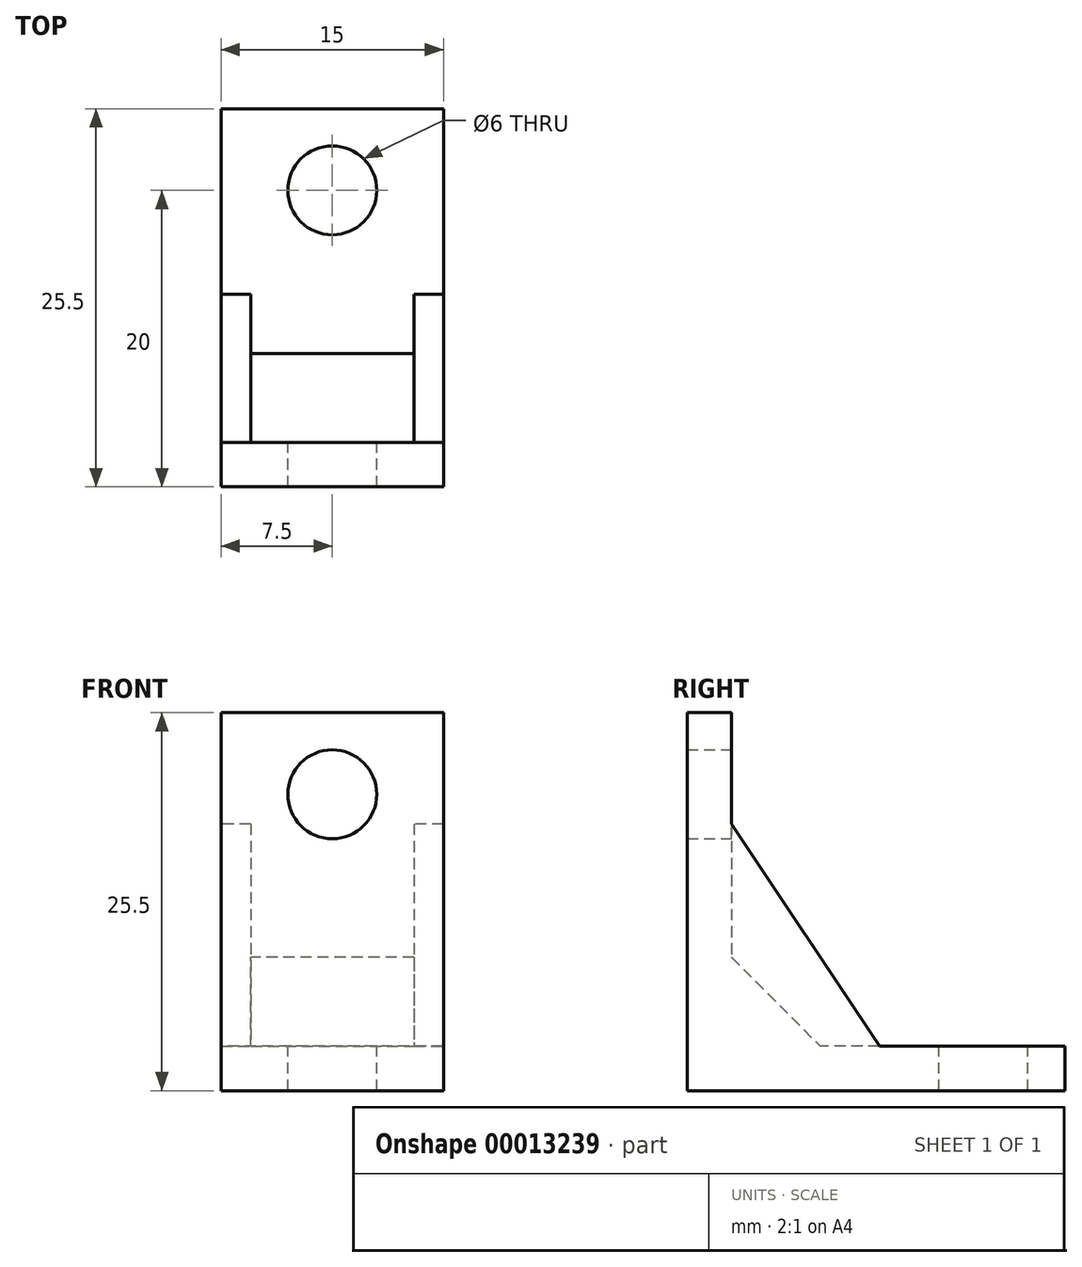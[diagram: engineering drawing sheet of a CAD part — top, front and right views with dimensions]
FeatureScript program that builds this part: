
annotation { "Feature Type Name" : "Feature", "Feature Type Description" : "" }
export const myFeature = defineFeature(function(context is Context, id is Id, definition is map)
    precondition{}
    {
        {
            var Q0;
            Q0=qCreatedBy(makeId("Right.planeOp"),FACE);
            var sketch = newSketch(context, id + "F0", { "sketchPlane" : qUnion([Q0])});
            skLineSegment(sketch, "E0", {"start": v(0, 25.5) * mm, "end": v(0, 0) * mm});
            skLineSegment(sketch, "E1", {"start": v(0, 0) * mm, "end": v(25.5, 0) * mm});
            skLineSegment(sketch, "E2", {"start": v(25.5, 0) * mm, "end": v(25.5, 3) * mm});
            skLineSegment(sketch, "E3", {"start": v(25.5, 3) * mm, "end": v(3, 3) * mm});
            skLineSegment(sketch, "E4", {"start": v(3, 3) * mm, "end": v(3, 25.5) * mm});
            skLineSegment(sketch, "E5", {"start": v(3, 25.5) * mm, "end": v(0, 25.5) * mm});
            skSolve(sketch);
        }
        {
            var Q0;
            Q0=qSketchRegion(id+"F0",true);
            extrude(context, id + "F1", {"entities" : qUnion([Q0]), "depth" : 15 * mm});
        }
        {
            var Q0;
            Q0=makeQuery(id+"F1.opExtrude","SWEPT_FACE",FACE,{"disambiguationData":[OSD([sQuery(id+"F0.wireOp",EDGE,"E4")])]});
            var sketch = newSketch(context, id + "F2", { "sketchPlane" : qUnion([Q0])});
            skPoint(sketch, "E6", {"position": v(-7.5, 20) * mm});
            skPoint(sketch, "E7", {"position": v(-7.5, 25.5) * mm});
            skSolve(sketch);
        }
        {
            var Q0;
            Q0=makeQuery(id+"F1.opExtrude","SWEPT_FACE",FACE,{"disambiguationData":[OSD([sQuery(id+"F0.wireOp",EDGE,"E3")])]});
            var sketch = newSketch(context, id + "F3", { "sketchPlane" : qUnion([Q0])});
            skPoint(sketch, "E8", {"position": v(7.5, 20) * mm});
            skSolve(sketch);
        }
        {
            var Q0;
            Q0=sQuery(id+"F3.wireOp",VERTEX,"E8");
            var Q1;
            Q1=sQuery(id+"F2.wireOp",VERTEX,"E6");
            var Q2;
            Q2=makeQuery(id+"F1.opExtrude","SWEPT_BODY",BODY,{"disambiguationData":[OSD([sQuery(id+"F0.wireOp",EDGE,"E0"),sQuery(id+"F0.wireOp",EDGE,"E1"),sQuery(id+"F0.wireOp",EDGE,"E2"),sQuery(id+"F0.wireOp",EDGE,"E3"),sQuery(id+"F0.wireOp",EDGE,"E4"),sQuery(id+"F0.wireOp",EDGE,"E5")])]});
            hole(context, id + "F4", {"style" : HoleStyle.SIMPLE, "endStyle" : HoleEndStyle.THROUGH, "holeDiameter" : 6 * mm, "locations" : qUnion([Q0, Q1]), "scope" : qUnion([Q2]), "isTappedThrough" : true});
        }
        {
            var Q0;
            Q0=makeQuery(id+"F1.opExtrude","SWEPT_EDGE",EDGE,{"disambiguationData":[OSD([sQuery(id+"F0.wireOp",EDGE,"E3"),sQuery(id+"F0.wireOp",EDGE,"E4")])]});
            chamfer(context, id + "F5", {"entities" : qUnion([Q0]), "chamferType" : ChamferType.TWO_OFFSETS, "width1" : 15 * mm, "oppositeDirection" : false, "width2" : 10 * mm, "tangentPropagation" : true});
        }
        {
            var Q0;
            Q0=makeQuery(id+"F1.opExtrude","SWEPT_FACE",FACE,{"disambiguationData":[OSD([sQuery(id+"F0.wireOp",EDGE,"E3")])]});
            var sketch = newSketch(context, id + "F6", { "sketchPlane" : qUnion([Q0])});
            skLineSegment(sketch, "E9.bottom", {"start": v(13, 25.5) * mm, "end": v(2, 25.5) * mm});
            skLineSegment(sketch, "E9.top", {"start": v(13, 3) * mm, "end": v(2, 3) * mm});
            skLineSegment(sketch, "E9.left", {"start": v(13, 25.5) * mm, "end": v(13, 3) * mm});
            skLineSegment(sketch, "E9.right", {"start": v(2, 25.5) * mm, "end": v(2, 3) * mm});
            skPoint(sketch, "E10", {"position": v(7.5, 25.5) * mm});
            skSolve(sketch);
        }
        {
            var Q0;
            Q0=qSketchRegion(id+"F6",true);
            extrude(context, id + "F7", {"entities" : qUnion([Q0]), "operationType" : NewBodyOperationType.REMOVE, "endBound" : BoundingType.THROUGH_ALL, "depth" : 25 * mm});
        }
        {
            var Q0;
            Q0=makeQuery(id+"F7.boolean.opBoolean","COPY",EDGE,{"derivedFrom":makeQuery(id+"F7.opExtrude","CAP_EDGE",EDGE,{"disambiguationData":[OSD([sQuery(id+"F6.wireOp",EDGE,"E9.top")])],"isStart":true})});
            chamfer(context, id + "F8", {"entities" : qUnion([Q0]), "width" : 6 * mm, "tangentPropagation" : true});
        }
    });
